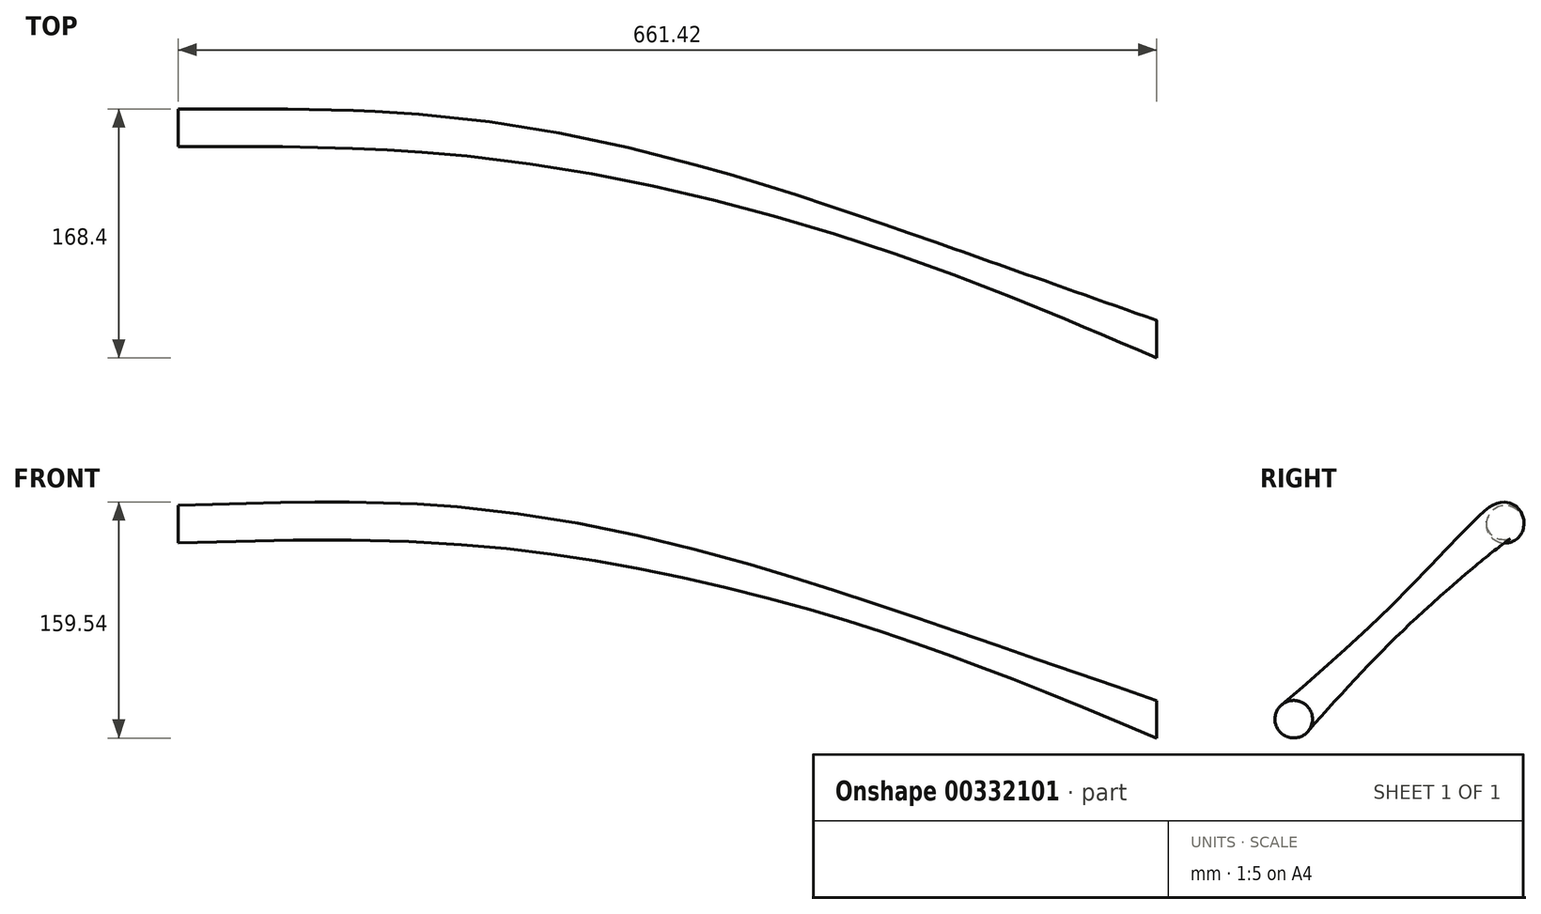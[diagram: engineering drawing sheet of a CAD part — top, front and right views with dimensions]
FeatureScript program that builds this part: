
annotation { "Feature Type Name" : "Feature", "Feature Type Description" : "" }
export const myFeature = defineFeature(function(context is Context, id is Id, definition is map)
    precondition{}
    {
        {
            var Q0;
            Q0=qCreatedBy(makeId("Right.planeOp"),FACE);
            cPlane(context, id + "F0", {"entities" : qUnion([Q0]), "cplaneType" : CPlaneType.OFFSET, "offset" : 177.3 * mm, "width" : 152.4 * mm, "height" : 152.4 * mm});
        }
        {
            var Q0;
            Q0=qCreatedBy(makeId("Right.planeOp"),FACE);
            var sketch = newSketch(context, id + "F1", { "sketchPlane" : qUnion([Q0])});
            skCircle(sketch, "E0", {"center": v(0, 0) * mm, "radius": 12.7 * mm});
            skSolve(sketch);
        }
        {
            var Q0;
            Q0=qCreatedBy(id+"F0.planeOp",FACE);
            var sketch = newSketch(context, id + "F2", { "sketchPlane" : qUnion([Q0])});
            skCircle(sketch, "E1", {"center": v(-4.72, 0) * mm, "radius": 12.7 * mm});
            skSolve(sketch);
        }
        {
            var Q0;
            Q0=qCreatedBy(makeId("Right.planeOp"),FACE);
            cPlane(context, id + "F3", {"entities" : qUnion([Q0]), "cplaneType" : CPlaneType.OFFSET, "offset" : 661.42 * mm, "width" : 152.4 * mm, "height" : 152.4 * mm});
        }
        {
            var Q0;
            Q0=qCreatedBy(id+"F3.planeOp",FACE);
            var sketch = newSketch(context, id + "F4", { "sketchPlane" : qUnion([Q0])});
            skCircle(sketch, "E2", {"center": v(-142.85, -131.77) * mm, "radius": 12.7 * mm});
            skSolve(sketch);
        }
        {
            var Q0;
            Q0=makeQuery(id+"F1.imprint","IMPRINT",FACE,{"disambiguationData":[TD([[makeQuery(id+"F1.imprint","IMPRINT",EDGE,{"derivedFrom":sQuery(id+"F1.wireOp",EDGE,"E0")}),1.0]])]});
            var Q1;
            Q1=makeQuery(id+"F2.imprint","IMPRINT",FACE,{"disambiguationData":[TD([[makeQuery(id+"F2.imprint","IMPRINT",EDGE,{"derivedFrom":sQuery(id+"F2.wireOp",EDGE,"E1")}),1.0]])]});
            var Q2;
            Q2=makeQuery(id+"F4.imprint","IMPRINT",FACE,{"disambiguationData":[TD([[makeQuery(id+"F4.imprint","IMPRINT",EDGE,{"derivedFrom":sQuery(id+"F4.wireOp",EDGE,"E2")}),1.0]])]});
            loft(context, id + "F5", {"sheetProfilesArray" : [{ "sheetProfileEntities" : qUnion([Q0]) }, { "sheetProfileEntities" : qUnion([Q1]) }, { "sheetProfileEntities" : qUnion([Q2]) }]});
        }
    });
